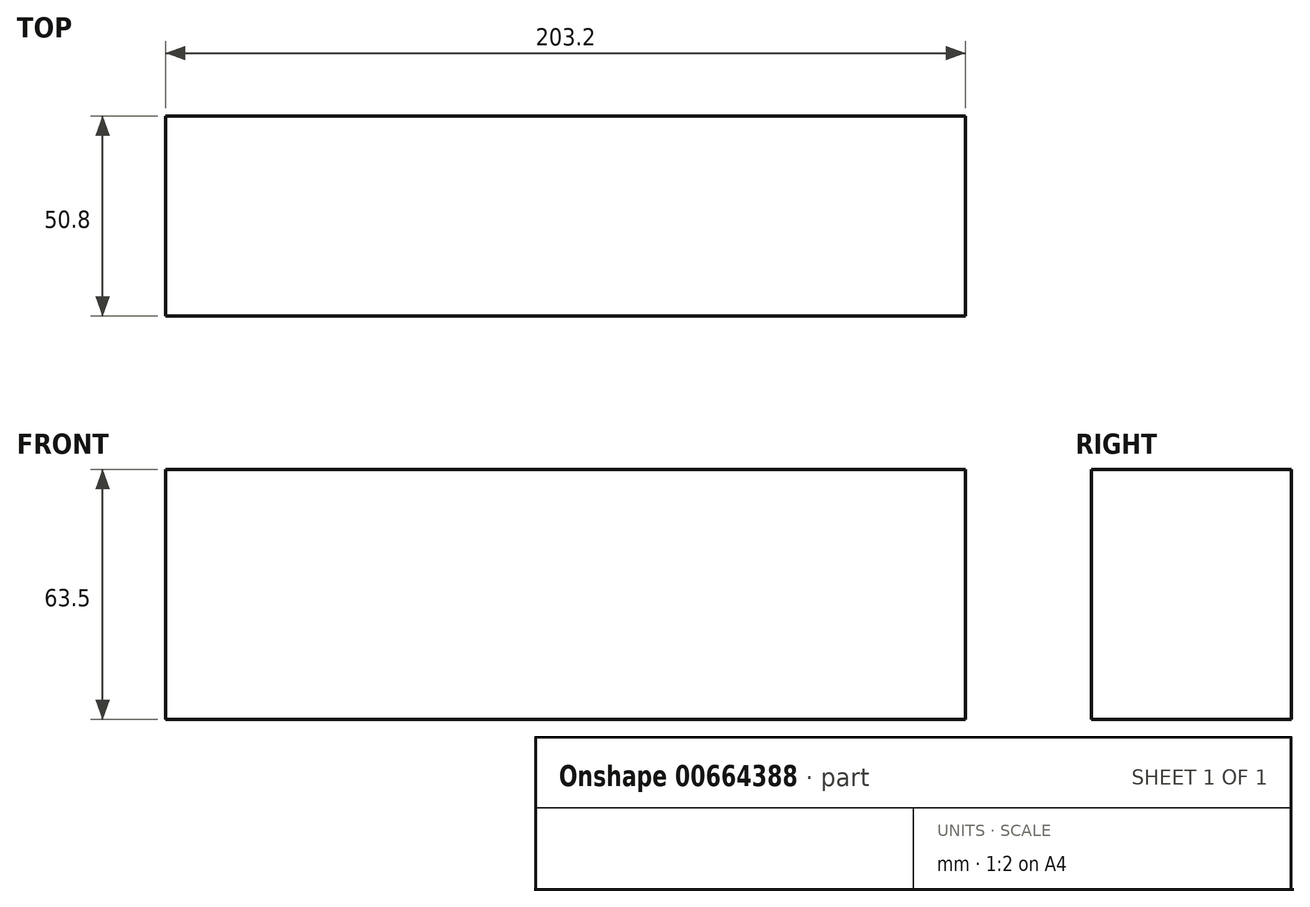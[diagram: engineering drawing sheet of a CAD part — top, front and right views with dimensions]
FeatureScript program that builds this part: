
annotation { "Feature Type Name" : "Feature", "Feature Type Description" : "" }
export const myFeature = defineFeature(function(context is Context, id is Id, definition is map)
    precondition{}
    {
        {
            var Q0;
            Q0=qCreatedBy(makeId("Front.planeOp"),FACE);
            var sketch = newSketch(context, id + "F0", { "sketchPlane" : qUnion([Q0])});
            skLineSegment(sketch, "E0.bottom", {"start": v(193.3, 0) * mm, "end": v(396.5, 0) * mm});
            skLineSegment(sketch, "E0.top", {"start": v(193.3, -63.5) * mm, "end": v(396.5, -63.5) * mm});
            skLineSegment(sketch, "E0.left", {"start": v(193.3, 0) * mm, "end": v(193.3, -63.5) * mm});
            skLineSegment(sketch, "E0.right", {"start": v(396.5, 0) * mm, "end": v(396.5, -63.5) * mm});
            skSolve(sketch);
        }
        {
            var Q0;
            Q0=makeQuery(id+"F0.imprint","IMPRINT",FACE,{"disambiguationData":[TD([[makeQuery(id+"F0.imprint","IMPRINT",EDGE,{"derivedFrom":sQuery(id+"F0.wireOp",EDGE,"E0.bottom")}),-1.0]])]});
            extrude(context, id + "F1", {"entities" : qUnion([Q0]), "oppositeDirection" : true, "depth" : 50.8 * mm, "offsetDistance" : 25.4 * mm});
        }
    });
